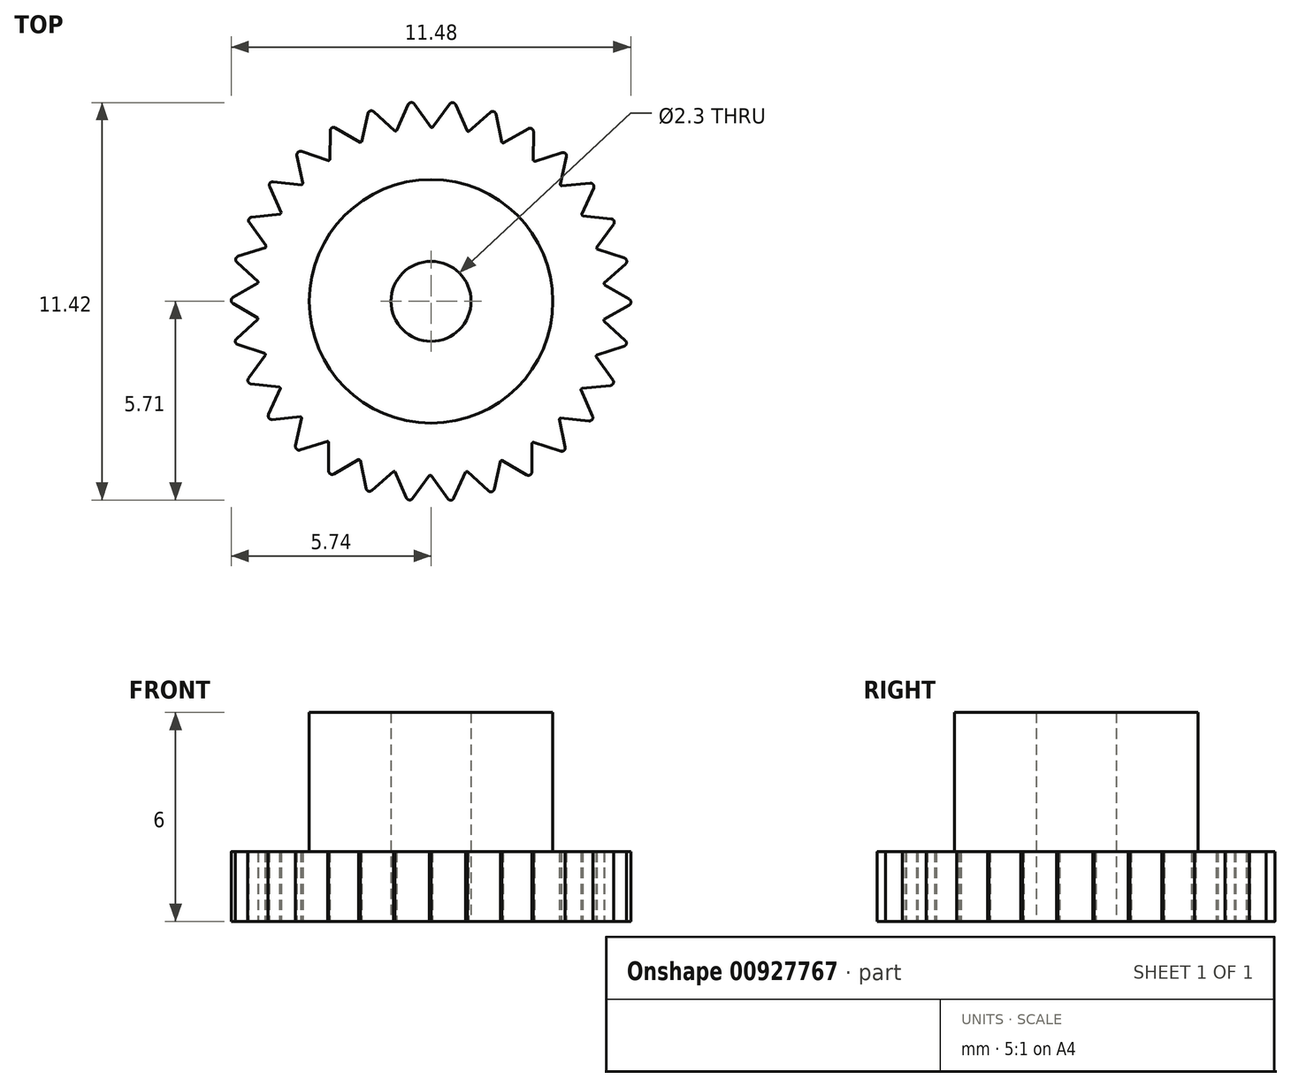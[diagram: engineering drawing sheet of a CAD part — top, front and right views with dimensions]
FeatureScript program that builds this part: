
annotation { "Feature Type Name" : "Feature", "Feature Type Description" : "" }
export const myFeature = defineFeature(function(context is Context, id is Id, definition is map)
    precondition{}
    {
        {
            var Q0;
            Q0=qCreatedBy(makeId("Top.planeOp"),FACE);
            var sketch = newSketch(context, id + "F0", { "sketchPlane" : qUnion([Q0])});
            skArc(sketch, "E0", {"start": v(-1, 4.9) * mm, "mid": v(0.5, -4.97) * mm, "end": v(0, 5) * mm});
            skCircle(sketch, "E1", {"center": v(0, 0) * mm, "radius": 3.5 * mm});
            skLineSegment(sketch, "E2", {"start": v(-1, 4.9) * mm, "end": v(0, 5) * mm});
            skLineSegment(sketch, "E3", {"start": v(-1, 4.9) * mm, "end": v(-0.66, 5.65) * mm});
            skLineSegment(sketch, "E4", {"start": v(-0.48, 5.67) * mm, "end": v(0, 5) * mm});
            skCircle(sketch, "E5", {"center": v(0, 0) * mm, "radius": 1.15 * mm});
            skPoint(sketch, "E6.visualSharp", {"position": v(-0.58, 5.81) * mm});
            skArc(sketch, "E6.filletArc", {"start": v(-0.48, 5.67) * mm, "mid": v(-0.57, 5.71) * mm, "end": v(-0.66, 5.65) * mm});
            skSolve(sketch);
        }
        {
            var Q0;
            Q0=qCreatedBy(makeId("Front.planeOp"),FACE);
            var sketch = newSketch(context, id + "F1", { "sketchPlane" : qUnion([Q0])});
            skLineSegment(sketch, "E7", {"start": v(0, 0) * mm, "end": v(0, 26.77) * mm, "construction": true});
            skSolve(sketch);
        }
        {
            var Q0;
            Q0=makeQuery(id+"F0.imprint","IMPRINT",FACE,{"disambiguationData":[TD([[makeQuery(id+"F0.imprint","IMPRINT",EDGE,{"derivedFrom":sQuery(id+"F0.wireOp",EDGE,"E1")}),1.0]])]});
            extrude(context, id + "F2", {"entities" : qUnion([Q0]), "depth" : 5 * mm, "offsetDistance" : 25 * mm});
        }
        {
            var Q0;
            Q0=makeQuery(id+"F0.imprint","IMPRINT",FACE,{"disambiguationData":[TD([[makeQuery(id+"F0.imprint","IMPRINT",EDGE,{"derivedFrom":sQuery(id+"F0.wireOp",EDGE,"E1")}),1.0]])]});
            extrude(context, id + "F3", {"entities" : qUnion([Q0]), "operationType" : NewBodyOperationType.ADD, "oppositeDirection" : true, "depth" : 1 * mm, "offsetDistance" : 25 * mm});
        }
        {
            var Q0;
            Q0=makeQuery(id+"F0.imprint","IMPRINT",FACE,{"disambiguationData":[TD([[makeQuery(id+"F0.imprint","IMPRINT",EDGE,{"derivedFrom":sQuery(id+"F0.wireOp",EDGE,"E1")}),-1.0]])]});
            extrude(context, id + "F4", {"entities" : qUnion([Q0]), "operationType" : NewBodyOperationType.ADD, "endBound" : BoundingType.SYMMETRIC, "depth" : 2 * mm, "offsetDistance" : 25 * mm});
        }
        {
            var Q0;
            {var subQ5=sQuery(id+"F0.wireOp",EDGE,"E3");Q0=makeQuery(id+"F0.imprint","IMPRINT",FACE,{"disambiguationData":[TD([[makeQuery(id+"F0.imprint","IMPRINT",EDGE,{"derivedFrom":subQ5}),-1.0]])]});}
            extrude(context, id + "F5", {"entities" : qUnion([Q0]), "endBound" : BoundingType.SYMMETRIC, "depth" : 2 * mm, "offsetDistance" : 25 * mm});
        }
        {
            var Q0;
            Q0=makeQuery(id+"F5.opExtrude","SWEPT_BODY",BODY,{"disambiguationData":[OSD([sQuery(id+"F0.wireOp",EDGE,"E2"),sQuery(id+"F0.wireOp",EDGE,"E3"),sQuery(id+"F0.wireOp",EDGE,"E4")])]});
            var Q1;
            Q1=sQuery(id+"F1.wireOp",EDGE,"E7");
            circularPattern(context, id + "F6", {"operationType" : NewBodyOperationType.ADD, "entities" : qUnion([Q0]), "axis" : qUnion([Q1]), "angle" : 360 * degree, "instanceCount" : 30, "equalSpace" : true});
        }
        {
            var Q0;
            Q0=qCreatedBy(makeId("Front.planeOp"),FACE);
            cPlane(context, id + "F7", {"entities" : qUnion([Q0]), "cplaneType" : CPlaneType.OFFSET, "offset" : 8.8 * mm, "width" : 150 * mm, "height" : 150 * mm});
        }
    });
